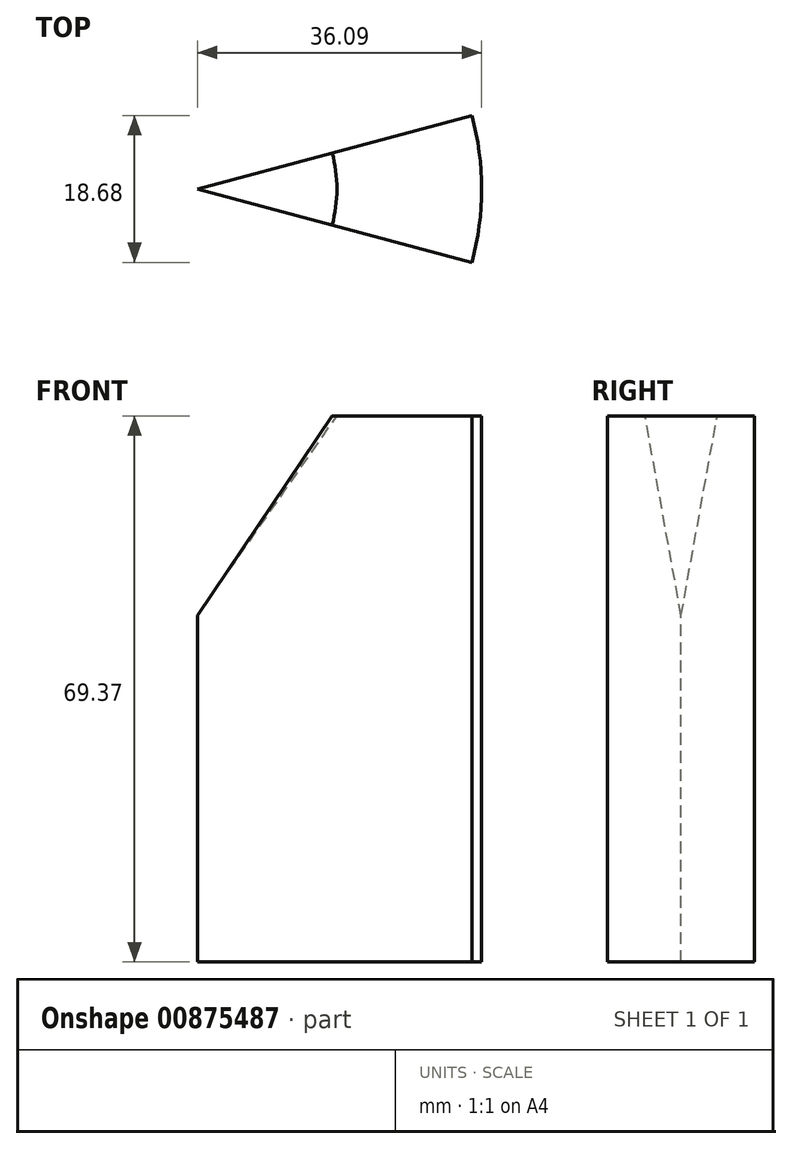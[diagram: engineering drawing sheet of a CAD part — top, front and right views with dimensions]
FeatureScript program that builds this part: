
annotation { "Feature Type Name" : "Feature", "Feature Type Description" : "" }
export const myFeature = defineFeature(function(context is Context, id is Id, definition is map)
    precondition{}
    {
        {
            var Q0;
            Q0=qCreatedBy(makeId("Front.planeOp"),FACE);
            var sketch = newSketch(context, id + "F0", { "sketchPlane" : qUnion([Q0])});
            skLineSegment(sketch, "E0", {"start": v(0, 0) * mm, "end": v(0, 44.02) * mm});
            skLineSegment(sketch, "E1", {"start": v(0, 44.02) * mm, "end": v(17.7, 69.37) * mm});
            skLineSegment(sketch, "E2", {"start": v(17.7, 69.37) * mm, "end": v(36.09, 69.37) * mm});
            skLineSegment(sketch, "E3", {"start": v(36.09, 69.37) * mm, "end": v(36.09, 0) * mm});
            skLineSegment(sketch, "E4", {"start": v(36.09, 0) * mm, "end": v(0, 0) * mm});
            skSolve(sketch);
        }
        {
            var Q0;
            Q0 = qSketchRegion(id + "F0", true);
            var Q1;
            Q1=sQuery(id+"F0.wireOp",EDGE,"E0");
            revolve(context, id + "F1", {"surfaceOperationType" : NewSurfaceOperationType.NEW, "entities" : qUnion([Q0]), "axis" : qUnion([Q1]), "revolveType" : RevolveType.SYMMETRIC, "angle" : 30 * degree});
        }
    });
